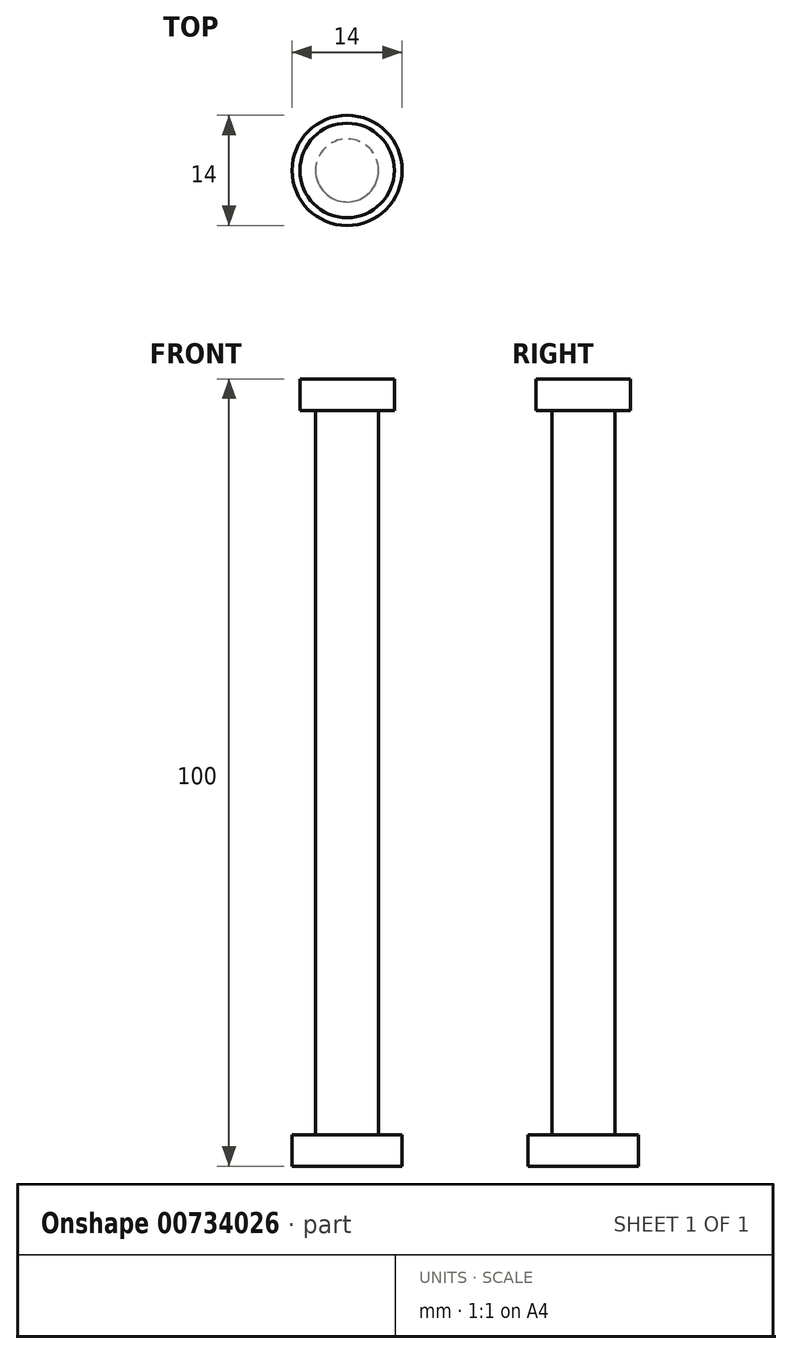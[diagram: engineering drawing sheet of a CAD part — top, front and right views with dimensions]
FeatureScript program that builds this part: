
annotation { "Feature Type Name" : "Feature", "Feature Type Description" : "" }
export const myFeature = defineFeature(function(context is Context, id is Id, definition is map)
    precondition{}
    {
        {
            var Q0;
            Q0=qCreatedBy(makeId("Top.planeOp"),FACE);
            var sketch = newSketch(context, id + "F0", { "sketchPlane" : qUnion([Q0])});
            skCircle(sketch, "E0", {"center": v(0, 0) * mm, "radius": 4 * mm});
            skSolve(sketch);
        }
        {
            var Q0;
            Q0 = qSketchRegion(id + "F0", true);
            extrude(context, id + "F1", {"entities" : qUnion([Q0]), "endBound" : BoundingType.SYMMETRIC, "depth" : 100 * mm, "offsetDistance" : 25 * mm});
        }
        {
            var Q0;
            Q0=makeQuery(id+"F1.opExtrude","CAP_FACE",FACE,{"disambiguationData":[OSD([sQuery(id+"F0.wireOp",EDGE,"E0")])],"isStart":false});
            var sketch = newSketch(context, id + "F2", { "sketchPlane" : qUnion([Q0])});
            skCircle(sketch, "E1", {"center": v(0, 0) * mm, "radius": 6 * mm});
            skSolve(sketch);
        }
        {
            var Q0;
            Q0 = qSketchRegion(id + "F2", true);
            extrude(context, id + "F3", {"entities" : qUnion([Q0]), "operationType" : NewBodyOperationType.ADD, "oppositeDirection" : true, "depth" : 4 * mm, "offsetDistance" : 25 * mm});
        }
        {
            var Q0;
            Q0=makeQuery(id+"F1.opExtrude","CAP_FACE",FACE,{"disambiguationData":[OSD([sQuery(id+"F0.wireOp",EDGE,"E0")])],"isStart":true});
            var sketch = newSketch(context, id + "F4", { "sketchPlane" : qUnion([Q0])});
            skCircle(sketch, "E2", {"center": v(0, 0) * mm, "radius": 7 * mm});
            skSolve(sketch);
        }
        {
            var Q0;
            Q0 = qSketchRegion(id + "F4", true);
            extrude(context, id + "F5", {"entities" : qUnion([Q0]), "operationType" : NewBodyOperationType.ADD, "oppositeDirection" : true, "depth" : 4 * mm, "offsetDistance" : 25 * mm});
        }
    });
